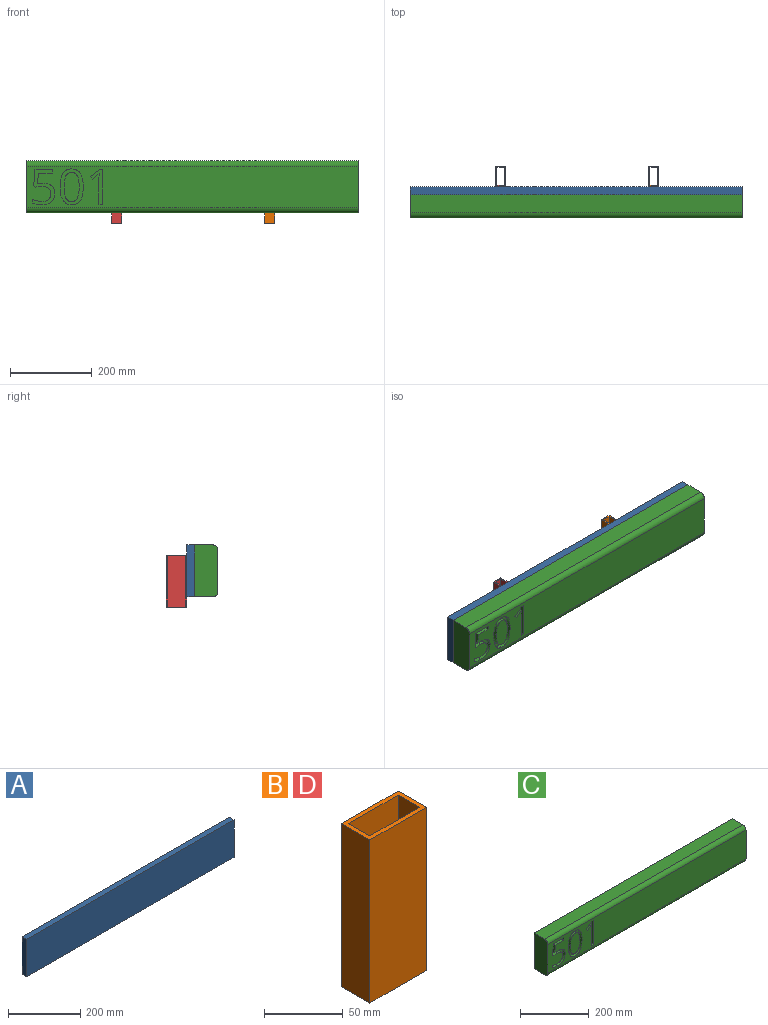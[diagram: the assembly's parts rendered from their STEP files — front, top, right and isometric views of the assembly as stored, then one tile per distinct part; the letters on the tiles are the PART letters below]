
ASSEMBLY  parts=4 mates=3
PART A: 6 faces, bbox 812.8x19.1x127 mm
  f0: plane 127x19.05mm, normal (1,0,0), area 2419.3mm2, adj f1,f3,f4,f5
  f1: plane 812.8x19.05mm, normal (0,0,1), area 15483.8mm2, adj f0,f2,f4,f5
  f2: plane 127x19.05mm, normal (-1,0,0), area 2419.3mm2, adj f1,f3,f4,f5
  f3: plane 812.8x19.05mm, normal (0,0,-1), area 15483.8mm2, adj f0,f2,f4,f5
  f4: plane 812.8x127mm, normal (0,-1,0), area 103225.6mm2, adj f0,f1,f2,f3
  f5: plane 812.8x127mm, normal (0,1,0), area 103225.6mm2, adj f0,f1,f2,f3
PART B: 10 faces, bbox 50.8x25.4x127 mm
  f0: plane 127x19.05mm, normal (1,0,0), area 2419.3mm2, adj f1,f7,f8,f9
  f1: plane 127x44.45mm, normal (0,-1,0), area 5645.2mm2, adj f0,f2,f8,f9
  f2: plane 127x19.05mm, normal (-1,0,0), area 2419.3mm2, adj f1,f7,f8,f9
  f3: plane 127x25.4mm, normal (1,0,0), area 3225.8mm2, adj f4,f6,f8,f9
  f4: plane 127x50.8mm, normal (0,1,0), area 6451.6mm2, adj f3,f5,f8,f9
  f5: plane 127x25.4mm, normal (-1,0,0), area 3225.8mm2, adj f4,f6,f8,f9
  f6: plane 127x50.8mm, normal (0,-1,0), area 6451.6mm2, adj f3,f5,f8,f9
  f7: plane 127x44.45mm, normal (0,1,0), area 5645.2mm2, adj f0,f2,f8,f9
  f8: plane 50.8x25.4mm, normal (0,0,1), area 443.5mm2, adj f0,f1,f2,f3,f4,f5,f6,f7
  f9: plane 50.8x25.4mm, normal (0,0,-1), area 443.5mm2, adj f0,f1,f2,f3,f4,f5,f6,f7
PART C: 56 faces, bbox 812.8x57.2x127 mm
  f0: plane 812.8x101.6mm, normal (0,-1,0), area 75725.7mm2, adj f1,f3,f6,f7,f15,f16,f17,f18
  f1: plane 127x57.15mm, normal (1,0,0), area 7188.8mm2, adj f0,f2,f4,f5,f6,f7
  f2: plane 812.8x44.45mm, normal (0,0,1), area 36129mm2, adj f1,f3,f5,f6
  f3: plane 127x57.15mm, normal (-1,0,0), area 7188.8mm2, adj f0,f2,f4,f5,f6,f7
  f4: plane 812.8x44.45mm, normal (0,0,-1), area 36129mm2, adj f1,f3,f5,f7
  f5: plane 812.8x127mm, normal (0,1,0), area 103225.6mm2, adj f1,f2,f3,f4
  f6: cylinder r=12.7mm len=812.8mm, axis (1,0,0), area 16214.6mm2, adj f0,f1,f2,f3
  f7: cylinder r=12.7mm len=812.8mm, axis (-1,0,0), area 16214.6mm2, adj f0,f1,f3,f4
  f8: extruded ~27.2x10.16mm, area 282.3mm2, adj f9,f23,f24,f55
  f9: extruded ~27.14x10.16mm, area 281.6mm2, adj f8,f10,f24,f55
  f10: extruded ~13.98x10.16mm, area 175.8mm2, adj f9,f11,f24,f55
  f11: extruded ~14.08x10.16mm, area 177.5mm2, adj f10,f12,f24,f55
  f12: extruded ~27.01x10.16mm, area 280.3mm2, adj f11,f13,f24,f55
  f13: extruded ~27.09x10.16mm, area 281mm2, adj f12,f14,f24,f55
  f14: extruded ~14.08x10.16mm, area 177.9mm2, adj f13,f23,f24,f55
  f15: extruded ~33.15x10.16mm, area 348.6mm2, adj f0,f16,f22,f24
  f16: extruded ~32.72x10.16mm, area 344.9mm2, adj f0,f15,f17,f24
  f17: extruded ~21.17x11.31mm, area 255.5mm2, adj f0,f16,f18,f24
  f18: extruded ~21.24x10.84mm, area 253.8mm2, adj f0,f17,f19,f24
  f19: extruded ~33.19x10.16mm, area 348.9mm2, adj f0,f18,f20,f24
  f20: extruded ~32.89x10.16mm, area 346.5mm2, adj f0,f19,f21,f24
  f21: extruded ~21.01x11.21mm, area 253.5mm2, adj f0,f20,f22,f24
  f22: extruded ~21.4x10.95mm, area 255.9mm2, adj f0,f15,f21,f24
  f23: extruded ~13.98x10.16mm, area 176.2mm2, adj f8,f14,f24,f55
  f24: plane 88.12x56.61mm, normal (0,-1,0), area 1934.7mm2, adj f8,f9,f10,f11,f12,f13,f14,f15
  f25: plane 10.16x9.48mm, normal (0,0,1), area 96.3mm2, adj f0,f26,f33,f34
  f26: plane 85.59x10.16mm, normal (-1,0,0), area 869.6mm2, adj f0,f25,f27,f34
  f27: plane 10.16x8.19mm, normal (0,0,-1), area 83.2mm2, adj f0,f26,f28,f34
  f28: plane 22.65x17.52mm, normal (0.61,0,-0.79), area 290.9mm2, adj f0,f27,f29,f34
  f29: plane 10.16x6.67mm, normal (0.79,0,0.61), area 85.6mm2, adj f0,f28,f30,f34
  f30: extruded ~13.93x11.42mm, area 183mm2, adj f0,f29,f31,f34
  f31: extruded ~10.16x2.74mm, area 38.2mm2, adj f0,f30,f32,f34
  f32: extruded ~14.41x10.16mm, area 146.5mm2, adj f0,f31,f33,f34
  f33: plane 61x10.16mm, normal (1,0,0), area 619.7mm2, adj f0,f25,f32,f34
  f34: plane 85.59x30.84mm, normal (0,-1,0), area 1002.8mm2, adj f25,f26,f27,f28,f29,f30,f31,f32
  f35: extruded ~21.28x10.16mm, area 231.7mm2, adj f0,f36,f53,f54
  f36: extruded ~13.41x10.16mm, area 137.2mm2, adj f0,f35,f37,f54
  f37: plane 25.7x10.16mm, normal (-1,0,0.08), area 262.1mm2, adj f0,f36,f38,f54
  f38: plane 34.24x10.16mm, normal (0,0,1), area 347.9mm2, adj f0,f37,f39,f54
  f39: plane 10.16x8.95mm, normal (-1,0,0), area 91mm2, adj f0,f38,f40,f54
  f40: plane 42.56x10.16mm, normal (0,0,-1), area 432.4mm2, adj f0,f39,f41,f54
  f41: plane 40.05x10.16mm, normal (1,0,-0.08), area 408.2mm2, adj f0,f40,f42,f54
  f42: plane 10.16x5.04mm, normal (0.54,0,0.84), area 60.8mm2, adj f0,f41,f43,f54
  f43: extruded ~14.87x10.16mm, area 152.3mm2, adj f0,f42,f44,f54
  f44: extruded ~21.94x17.91mm, area 329.2mm2, adj f0,f43,f45,f54
  f45: extruded ~14.06x10.16mm, area 159.4mm2, adj f0,f44,f46,f54
  f46: extruded ~16.01x10.16mm, area 173.6mm2, adj f0,f45,f47,f54
  f47: extruded ~12.01x10.16mm, area 123.2mm2, adj f0,f46,f48,f54
  f48: extruded ~10.17x10.16mm, area 112mm2, adj f0,f47,f49,f54
  f49: plane 10.16x9.37mm, normal (1,0,0), area 95.2mm2, adj f0,f48,f50,f54
  f50: extruded ~22.07x10.16mm, area 231.8mm2, adj f0,f49,f51,f54
  f51: extruded ~23.33x10.16mm, area 254.9mm2, adj f0,f50,f52,f54
  f52: extruded ~20.84x10.16mm, area 235.9mm2, adj f0,f51,f53,f54
  f53: extruded ~18.36x10.16mm, area 209.3mm2, adj f0,f35,f52,f54
  f54: plane 86.77x53.86mm, normal (0,-1,0), area 1700.3mm2, adj f35,f36,f37,f38,f39,f40,f41,f42
  f55: plane 71.32x36.81mm, normal (0,-1,0), area 2217mm2, adj f8,f9,f10,f11,f12,f13,f14,f23
PART D: same geometry as B
PLACE A t=(-25.35,-28.05,-44.37)mm
PLACE B rot(axis=(0,0,1),90deg) t=(165.15,-2.65,-133.27)mm
PLACE C t=(-25.35,-28.05,-44.37)mm
PLACE D rot(axis=(0,0,1),90deg) t=(-209.6,-2.65,-133.27)mm
MATE fastened B.f5 <-> A.f5  axis (0,-1,0) through (177.85,-28.05,-6.27)mm
MATE fastened C.f5 <-> A.f4  axis (0,1,0) through (-25.35,-47.1,-44.37)mm
MATE fastened D.f5 <-> A.f5  axis (0,-1,0) through (-222.3,-28.05,-6.27)mm
